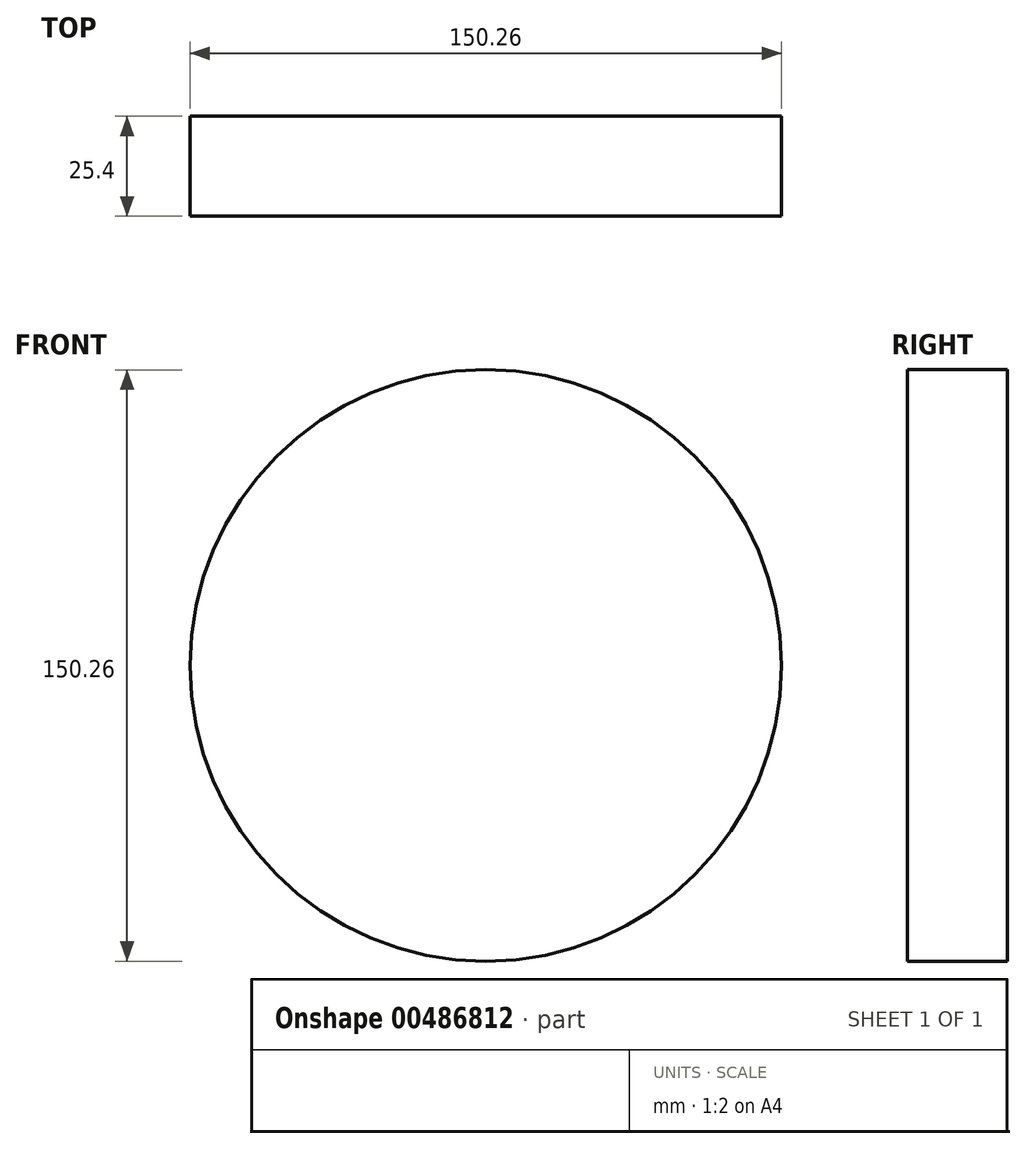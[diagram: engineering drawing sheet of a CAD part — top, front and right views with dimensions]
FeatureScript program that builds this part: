
annotation { "Feature Type Name" : "Feature", "Feature Type Description" : "" }
export const myFeature = defineFeature(function(context is Context, id is Id, definition is map)
    precondition{}
    {
        {
            var Q0;
            Q0=qCreatedBy(makeId("Front.planeOp"),FACE);
            var sketch = newSketch(context, id + "F0", { "sketchPlane" : qUnion([Q0])});
            skCircle(sketch, "E0", {"center": v(0, 0) * mm, "radius": 75.13 * mm});
            skCircle(sketch, "E1", {"center": v(0, 0) * mm, "radius": 58.27 * mm});
            skSolve(sketch);
        }
        {
            var Q0;
            Q0 = qSketchRegion(id + "F0", true);
            var Q1;
            Q1=makeQuery(id+"F0.imprint","IMPRINT",FACE,{"disambiguationData":[TD([[makeQuery(id+"F0.imprint","IMPRINT",EDGE,{"derivedFrom":sQuery(id+"F0.wireOp",EDGE,"E1")}),1.0]])]});
            extrude(context, id + "F1", {"entities" : qUnion([Q0, Q1]), "depth" : 25.4 * mm, "offsetDistance" : 25.4 * mm});
        }
    });
